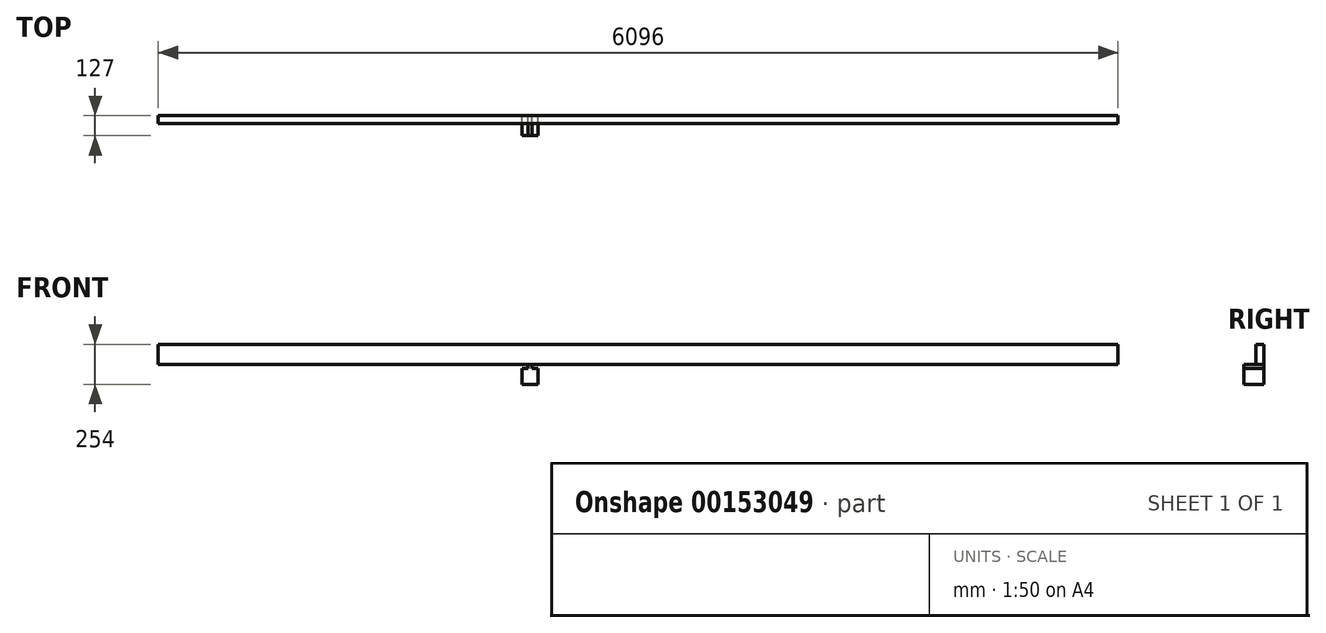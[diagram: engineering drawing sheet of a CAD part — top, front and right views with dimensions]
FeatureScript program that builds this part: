
annotation { "Feature Type Name" : "Feature", "Feature Type Description" : "" }
export const myFeature = defineFeature(function(context is Context, id is Id, definition is map)
    precondition{}
    {
        {
            var Q0;
            Q0=qCreatedBy(makeId("Front.planeOp"),FACE);
            var sketch = newSketch(context, id + "F0", { "sketchPlane" : qUnion([Q0])});
            skLineSegment(sketch, "E0.bottom", {"start": v(0, 0) * mm, "end": v(-6096, 0) * mm});
            skLineSegment(sketch, "E0.top", {"start": v(0, 127) * mm, "end": v(-6096, 127) * mm});
            skLineSegment(sketch, "E0.left", {"start": v(0, 0) * mm, "end": v(0, 127) * mm});
            skLineSegment(sketch, "E0.right", {"start": v(-6096, 0) * mm, "end": v(-6096, 127) * mm});
            skLineSegment(sketch, "E1", {"start": v(-3746.5, 0) * mm, "end": v(-3746.5, -25.4) * mm});
            skLineSegment(sketch, "E2", {"start": v(-3746.5, -25.4) * mm, "end": v(-3784.6, -25.4) * mm});
            skLineSegment(sketch, "E3", {"start": v(-3784.6, -25.4) * mm, "end": v(-3784.6, -127) * mm});
            skLineSegment(sketch, "E4", {"start": v(-3784.6, -127) * mm, "end": v(-3683, -127) * mm});
            skLineSegment(sketch, "E5", {"start": v(-3683, -127) * mm, "end": v(-3683, -25.4) * mm});
            skLineSegment(sketch, "E6", {"start": v(-3683, -25.4) * mm, "end": v(-3721.1, -25.4) * mm});
            skLineSegment(sketch, "E7", {"start": v(-3721.1, -25.4) * mm, "end": v(-3721.1, 0) * mm});
            skSolve(sketch);
        }
        {
            var Q0;
            Q0=makeQuery(id+"F0.imprint","IMPRINT",FACE,{"disambiguationData":[TD([[makeQuery(id+"F0.imprint","IMPRINT",EDGE,{"derivedFrom":sQuery(id+"F0.wireOp",EDGE,"E0.top")}),1.0]])]});
            extrude(context, id + "F1", {"entities" : qUnion([Q0]), "depth" : 50.8 * mm});
        }
        {
            var Q0;
            {var subQ0=sQuery(id+"F0.wireOp",EDGE,"E1");Q0=makeQuery(id+"F0.imprint","IMPRINT",FACE,{"disambiguationData":[TD([[makeQuery(id+"F0.imprint","IMPRINT",EDGE,{"derivedFrom":subQ0}),1.0]])]});}
            extrude(context, id + "F2", {"entities" : qUnion([Q0]), "operationType" : NewBodyOperationType.ADD, "depth" : 127 * mm});
        }
    });
